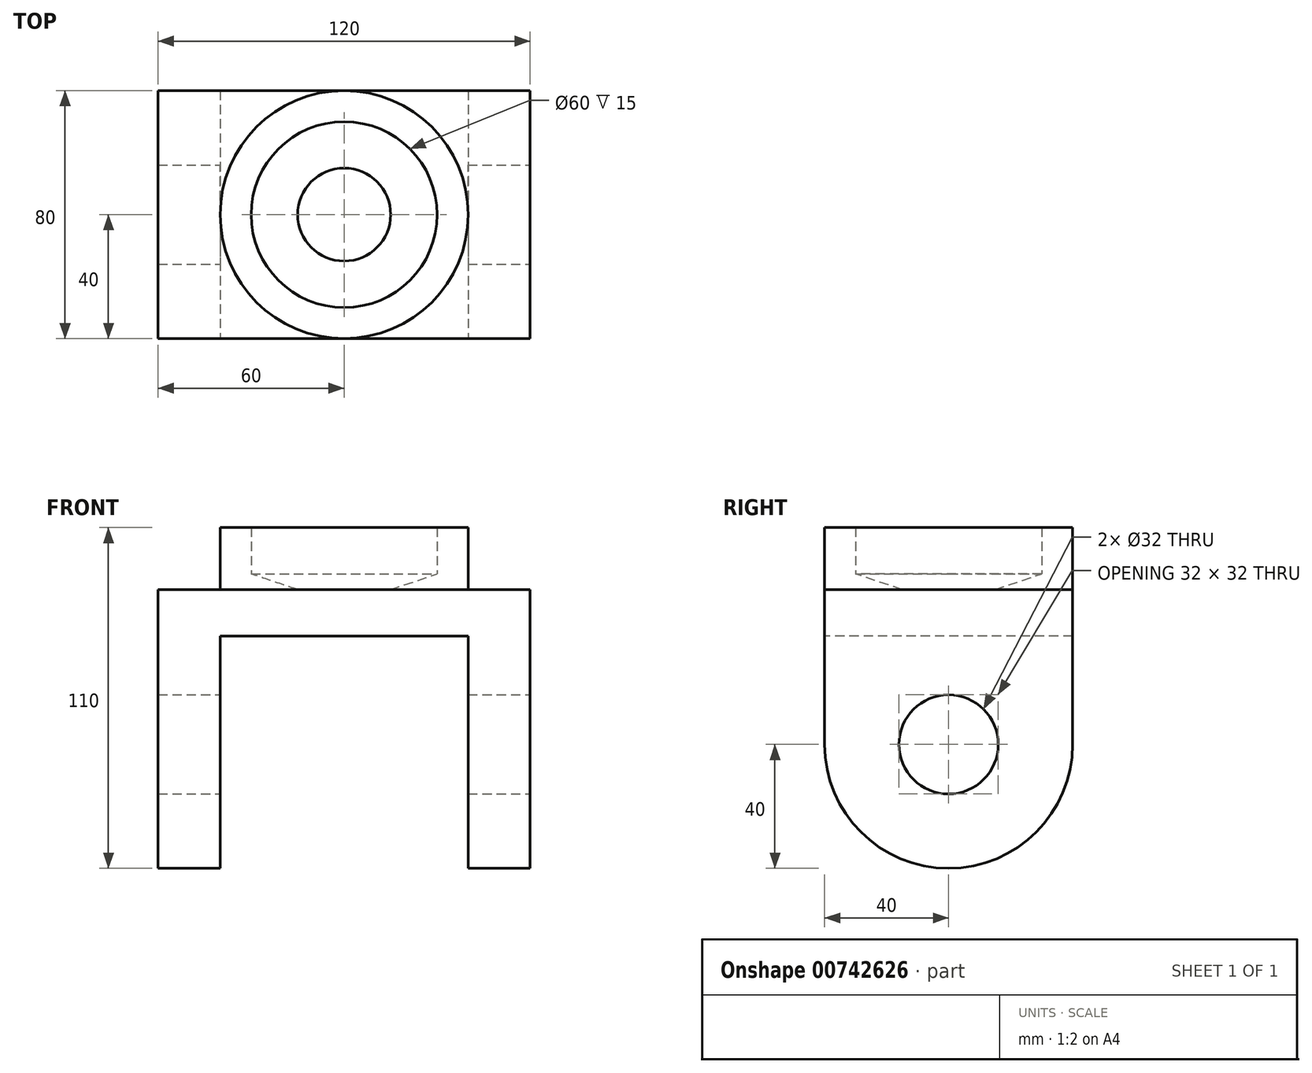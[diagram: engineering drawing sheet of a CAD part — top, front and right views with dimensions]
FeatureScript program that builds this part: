
annotation { "Feature Type Name" : "Feature", "Feature Type Description" : "" }
export const myFeature = defineFeature(function(context is Context, id is Id, definition is map)
    precondition{}
    {
        {
            var Q0;
            Q0=qCreatedBy(makeId("Top.planeOp"),FACE);
            var sketch = newSketch(context, id + "F0", { "sketchPlane" : qUnion([Q0])});
            skCircle(sketch, "E0", {"center": v(0, 0) * mm, "radius": 30 * mm});
            skCircle(sketch, "E1", {"center": v(0, 0) * mm, "radius": 40 * mm});
            skLineSegment(sketch, "E2.bottom", {"start": v(60, -40) * mm, "end": v(-60, -40) * mm});
            skLineSegment(sketch, "E2.top", {"start": v(60, 40) * mm, "end": v(-60, 40) * mm});
            skLineSegment(sketch, "E2.left", {"start": v(60, -40) * mm, "end": v(60, 40) * mm});
            skLineSegment(sketch, "E2.right", {"start": v(-60, -40) * mm, "end": v(-60, 40) * mm});
            skCircle(sketch, "E3", {"center": v(0, 0) * mm, "radius": 15 * mm});
            skSolve(sketch);
        }
        {
            var Q0;
            {var subQ5=sQuery(id+"F0.wireOp",EDGE,"E2.right");Q0=makeQuery(id+"F0.imprint","IMPRINT",FACE,{"disambiguationData":[TD([[makeQuery(id+"F0.imprint","IMPRINT",EDGE,{"derivedFrom":subQ5}),-1.0]])]});}
            var Q1;
            Q1=makeQuery(id+"F0.imprint","IMPRINT",FACE,{"disambiguationData":[TD([[makeQuery(id+"F0.imprint","IMPRINT",EDGE,{"derivedFrom":sQuery(id+"F0.wireOp",EDGE,"E0")}),-1.0]])]});
            var Q2;
            Q2=makeQuery(id+"F0.imprint","IMPRINT",FACE,{"disambiguationData":[TD([[makeQuery(id+"F0.imprint","IMPRINT",EDGE,{"derivedFrom":sQuery(id+"F0.wireOp",EDGE,"E0")}),1.0]])]});
            var Q3;
            Q3=makeQuery(id+"F0.imprint","IMPRINT",FACE,{"disambiguationData":[TD([[makeQuery(id+"F0.imprint","IMPRINT",EDGE,{"derivedFrom":sQuery(id+"F0.wireOp",EDGE,"E3")}),1.0]])]});
            var Q4;
            {var subQ5=sQuery(id+"F0.wireOp",EDGE,"E2.left");Q4=makeQuery(id+"F0.imprint","IMPRINT",FACE,{"disambiguationData":[TD([[makeQuery(id+"F0.imprint","IMPRINT",EDGE,{"derivedFrom":subQ5}),1.0]])]});}
            extrude(context, id + "F1", {"entities" : qUnion([Q0, Q1, Q2, Q3, Q4]), "oppositeDirection" : true, "depth" : 90 * mm, "offsetDistance" : 25 * mm});
        }
        {
            var Q0;
            Q0=makeQuery(id+"F1.opExtrude","SWEPT_FACE",FACE,{"disambiguationData":[OSD([sQuery(id+"F0.wireOp",EDGE,"E2.left")])]});
            var sketch = newSketch(context, id + "F2", { "sketchPlane" : qUnion([Q0])});
            skCircle(sketch, "E4", {"center": v(0, -50) * mm, "radius": 16 * mm});
            skCircle(sketch, "E5", {"center": v(0, -50) * mm, "radius": 40 * mm});
            skSolve(sketch);
        }
        {
            var Q0;
            Q0=makeQuery(id+"F2.imprint","IMPRINT",FACE,{"disambiguationData":[TD([[makeQuery(id+"F2.imprint","IMPRINT",EDGE,{"derivedFrom":sQuery(id+"F2.wireOp",EDGE,"E4")}),1.0]])]});
            var Q1;
            {var subQ0=sQuery(id+"F2.wireOp",EDGE,"E5");var subQ1=sQuery(id+"F0.wireOp",EDGE,"E2.left");var subQ4=makeQuery(id+"F1.opExtrude","CAP_EDGE",EDGE,{"disambiguationData":[OSD([subQ1])],"isStart":false});var subQ5=makeQuery(id+"F2.imprint","INTERSECT",VERTEX,{"derivedFrom":[subQ4,subQ0]});Q1=makeQuery(id+"F2.imprint","IMPRINT",FACE,{"disambiguationData":[TD([[makeQuery(id+"F2.imprint","IMPRINT",EDGE,{"disambiguationData":[TD([[subQ5,-1.0]])],"derivedFrom":subQ0}),-1.0]])]});}
            var Q2;
            {var subQ0=sQuery(id+"F2.wireOp",EDGE,"E5");var subQ1=sQuery(id+"F0.wireOp",EDGE,"E2.left");var subQ4=makeQuery(id+"F1.opExtrude","CAP_EDGE",EDGE,{"disambiguationData":[OSD([subQ1])],"isStart":false});var subQ5=makeQuery(id+"F2.imprint","INTERSECT",VERTEX,{"derivedFrom":[subQ4,subQ0]});Q2=makeQuery(id+"F2.imprint","IMPRINT",FACE,{"disambiguationData":[TD([[makeQuery(id+"F2.imprint","IMPRINT",EDGE,{"disambiguationData":[TD([[subQ5,1.0]])],"derivedFrom":subQ0}),-1.0]])]});}
            extrude(context, id + "F3", {"entities" : qUnion([Q0, Q1, Q2]), "operationType" : NewBodyOperationType.REMOVE, "oppositeDirection" : true, "depth" : 120 * mm, "offsetDistance" : 25 * mm});
        }
        {
            var Q0;
            Q0=makeQuery(id+"F1.opExtrude","SWEPT_FACE",FACE,{"disambiguationData":[OSD([sQuery(id+"F0.wireOp",EDGE,"E2.bottom")])]});
            var sketch = newSketch(context, id + "F4", { "sketchPlane" : qUnion([Q0])});
            skLineSegment(sketch, "E6.top", {"start": v(-40, -90) * mm, "end": v(40, -90) * mm});
            skLineSegment(sketch, "E6.left", {"start": v(-40, -15) * mm, "end": v(-40, -90) * mm});
            skLineSegment(sketch, "E6.right", {"start": v(40, -15) * mm, "end": v(40, -90) * mm});
            skLineSegment(sketch, "E7", {"start": v(-40, -15) * mm, "end": v(40, -15) * mm});
            skSolve(sketch);
        }
        {
            var Q0;
            {var subQ0=sQuery(id+"F4.wireOp",EDGE,"E7");Q0=makeQuery(id+"F4.imprint","IMPRINT",FACE,{"disambiguationData":[TD([[makeQuery(id+"F4.imprint","IMPRINT",EDGE,{"derivedFrom":subQ0}),-1.0]])]});}
            var Q1;
            {var subQ0=sQuery(id+"F4.wireOp",EDGE,"E6.top");Q1=makeQuery(id+"F4.imprint","IMPRINT",FACE,{"disambiguationData":[TD([[makeQuery(id+"F4.imprint","IMPRINT",EDGE,{"derivedFrom":subQ0}),1.0]])]});}
            extrude(context, id + "F5", {"entities" : qUnion([Q0, Q1]), "operationType" : NewBodyOperationType.REMOVE, "oppositeDirection" : true, "depth" : 250 * mm, "offsetDistance" : 25 * mm});
        }
        {
            var Q0;
            Q0=qCreatedBy(makeId("Front.planeOp"),FACE);
            var sketch = newSketch(context, id + "F6", { "sketchPlane" : qUnion([Q0])});
            skLineSegment(sketch, "E8", {"start": v(-15, 0) * mm, "end": v(-40, 0) * mm});
            skLineSegment(sketch, "E9", {"start": v(-40, 0) * mm, "end": v(-40, 20) * mm});
            skLineSegment(sketch, "E10", {"start": v(-40, 20) * mm, "end": v(-30, 20) * mm});
            skLineSegment(sketch, "E11", {"start": v(-30, 20) * mm, "end": v(-30, 5) * mm});
            skLineSegment(sketch, "E12", {"start": v(-30, 5) * mm, "end": v(-15, 0) * mm});
            skLineSegment(sketch, "E13", {"start": v(0, 0) * mm, "end": v(0, 47.65) * mm});
            skSolve(sketch);
        }
        {
            var Q0;
            Q0=makeQuery(id+"F6.imprint","IMPRINT",FACE,{"disambiguationData":[TD([[makeQuery(id+"F6.imprint","IMPRINT",EDGE,{"derivedFrom":sQuery(id+"F6.wireOp",EDGE,"E8")}),-1.0]])]});
            var Q1;
            Q1=sQuery(id+"F6.wireOp",EDGE,"E13");
            revolve(context, id + "F7", {"operationType" : NewBodyOperationType.ADD, "surfaceOperationType" : NewSurfaceOperationType.NEW, "entities" : qUnion([Q0]), "axis" : qUnion([Q1]), "revolveType" : RevolveType.FULL});
        }
    });
